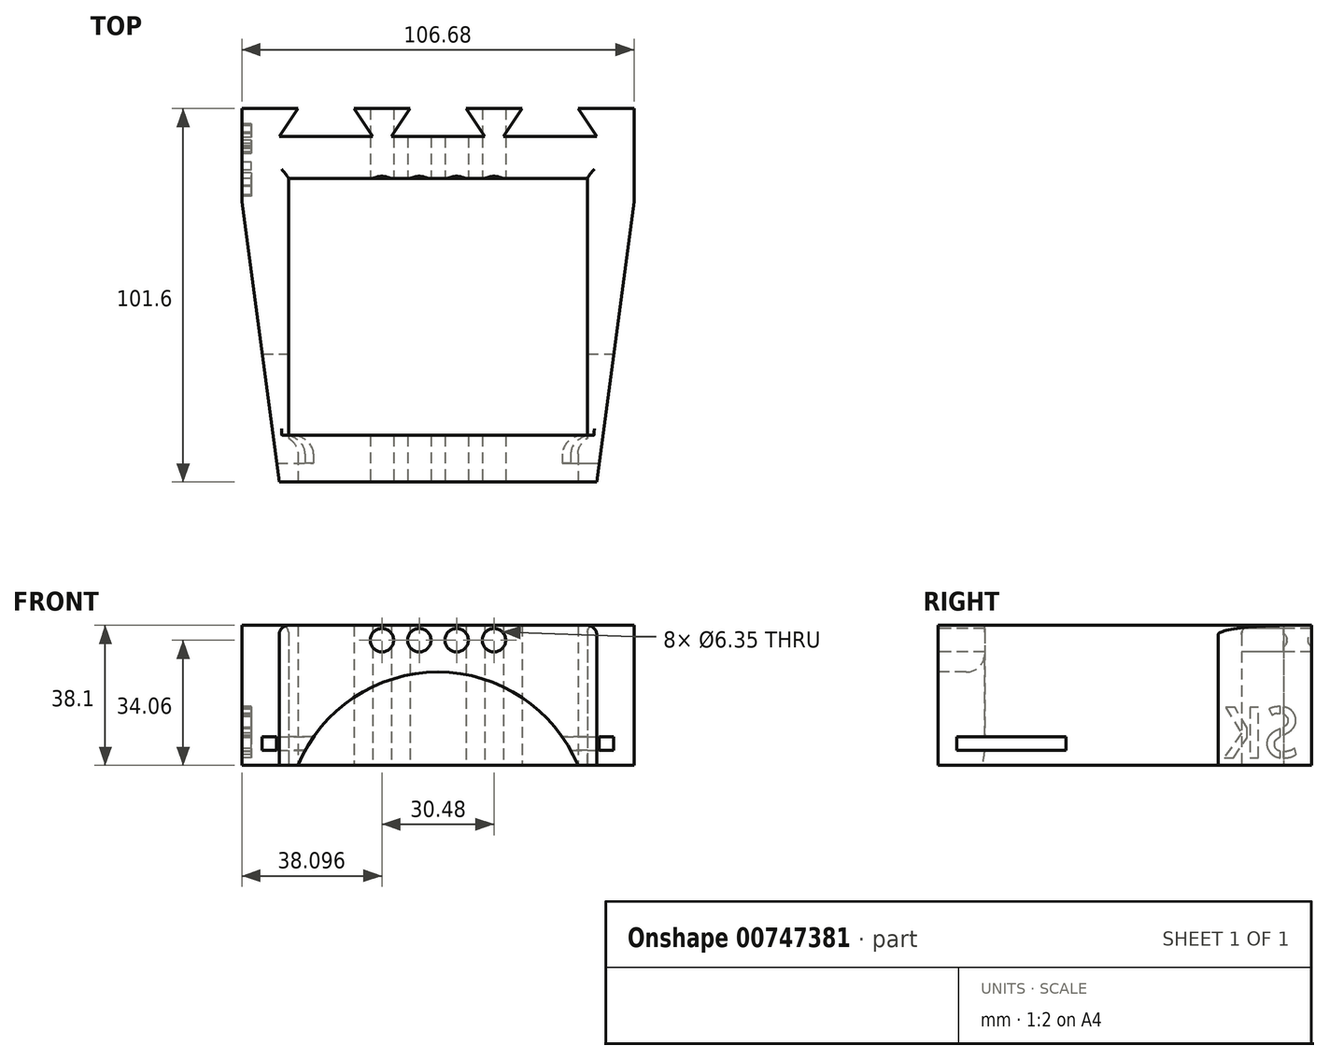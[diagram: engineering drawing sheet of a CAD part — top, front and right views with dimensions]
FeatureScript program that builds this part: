
annotation { "Feature Type Name" : "Feature", "Feature Type Description" : "" }
export const myFeature = defineFeature(function(context is Context, id is Id, definition is map)
    precondition{}
    {
        {
            var Q0;
            Q0=qCreatedBy(makeId("Top.planeOp"),FACE);
            var sketch = newSketch(context, id + "F0", { "sketchPlane" : qUnion([Q0])});
            skLineSegment(sketch, "E0.bottom", {"start": v(-50, 51.06) * mm, "end": v(-34.76, 51.06) * mm});
            skLineSegment(sketch, "E0.top", {"start": v(-50, -50.54) * mm, "end": v(56.68, -50.54) * mm});
            skLineSegment(sketch, "E0.left", {"start": v(-50, 51.06) * mm, "end": v(-50, -50.54) * mm});
            skLineSegment(sketch, "E0.right", {"start": v(56.68, 51.06) * mm, "end": v(56.68, -50.54) * mm});
            skLineSegment(sketch, "E1.bottom", {"start": v(-37.3, 32) * mm, "end": v(43.98, 32) * mm});
            skLineSegment(sketch, "E1.top", {"start": v(-37.3, -37.84) * mm, "end": v(43.98, -37.84) * mm});
            skLineSegment(sketch, "E1.left", {"start": v(-37.3, 32) * mm, "end": v(-37.3, -37.84) * mm});
            skLineSegment(sketch, "E1.right", {"start": v(43.98, 32) * mm, "end": v(43.98, -37.84) * mm});
            skLineSegment(sketch, "E2", {"start": v(-34.76, 51.06) * mm, "end": v(-39.84, 43.44) * mm});
            skLineSegment(sketch, "E3", {"start": v(-39.84, 43.44) * mm, "end": v(-14.44, 43.44) * mm});
            skLineSegment(sketch, "E4", {"start": v(-14.44, 43.44) * mm, "end": v(-19.52, 51.06) * mm});
            skLineSegment(sketch, "E5", {"start": v(-4.28, 51.06) * mm, "end": v(-9.36, 43.44) * mm});
            skLineSegment(sketch, "E6", {"start": v(-9.36, 43.44) * mm, "end": v(16.04, 43.44) * mm});
            skLineSegment(sketch, "E7", {"start": v(16.04, 43.44) * mm, "end": v(10.96, 51.06) * mm});
            skLineSegment(sketch, "E8", {"start": v(26.2, 51.06) * mm, "end": v(21.12, 43.44) * mm});
            skLineSegment(sketch, "E9", {"start": v(21.12, 43.44) * mm, "end": v(46.52, 43.44) * mm});
            skLineSegment(sketch, "E10", {"start": v(46.52, 43.44) * mm, "end": v(41.44, 51.06) * mm});
            skLineSegment(sketch, "E11.trimOffspring", {"start": v(-19.52, 51.06) * mm, "end": v(-4.28, 51.06) * mm});
            skLineSegment(sketch, "E12.trimOffspring", {"start": v(10.96, 51.06) * mm, "end": v(26.2, 51.06) * mm});
            skLineSegment(sketch, "E13.trimOffspring", {"start": v(41.44, 51.06) * mm, "end": v(56.68, 51.06) * mm});
            skSolve(sketch);
        }
        {
            var Q0;
            Q0=makeQuery(id+"F0.imprint","IMPRINT",FACE,{"disambiguationData":[TD([[makeQuery(id+"F0.imprint","IMPRINT",EDGE,{"derivedFrom":sQuery(id+"F0.wireOp",EDGE,"E0.bottom")}),-1.0]])]});
            extrude(context, id + "F1", {"entities" : qUnion([Q0]), "depth" : 38.1 * mm, "offsetDistance" : 25.4 * mm});
        }
        {
            var Q0;
            Q0=makeQuery(id+"F1.opExtrude","SWEPT_FACE",FACE,{"disambiguationData":[OSD([sQuery(id+"F0.wireOp",EDGE,"E0.top")])]});
            var sketch = newSketch(context, id + "F2", { "sketchPlane" : qUnion([Q0])});
            skArc(sketch, "E14", {"start": v(41.44, 0) * mm, "mid": v(3.34, 25.4) * mm, "end": v(-34.76, 0) * mm});
            skSolve(sketch);
        }
        {
            var Q0;
            {var subQ0=sQuery(id+"F2.wireOp",EDGE,"E14");Q0=makeQuery(id+"F2.imprint","IMPRINT",FACE,{"disambiguationData":[TD([[makeQuery(id+"F2.imprint","IMPRINT",EDGE,{"derivedFrom":subQ0}),1.0]])]});}
            extrude(context, id + "F3", {"entities" : qUnion([Q0]), "operationType" : NewBodyOperationType.REMOVE, "oppositeDirection" : true, "depth" : 25.4 * mm, "offsetDistance" : 25.4 * mm});
        }
        {
            var Q0;
            Q0=makeQuery(id+"F3.boolean.opBoolean","COPY",EDGE,{"derivedFrom":makeQuery(id+"F3.opExtrude","CAP_EDGE",EDGE,{"disambiguationData":[OSD([sQuery(id+"F2.wireOp",EDGE,"E14")])],"isStart":true})});
            var Q1;
            Q1=makeQuery(id+"F3.boolean.opBoolean","INTERSECT",EDGE,{"derivedFrom":[makeQuery(id+"F1.opExtrude","SWEPT_FACE",FACE,{"disambiguationData":[OSD([sQuery(id+"F0.wireOp",EDGE,"E1.top")])]}),makeQuery(id+"F3.opExtrude","SWEPT_FACE",FACE,{"disambiguationData":[OSD([sQuery(id+"F2.wireOp",EDGE,"E14")])]})]});
            fillet(context, id + "F4", {"entities" : qUnion([Q0, Q1]), "radius" : 5.08 * mm, "tangentPropagation" : true, "allowEdgeOverflow" : false});
        }
        {
            var Q0;
            Q0=makeQuery(id+"F1.opExtrude","SWEPT_EDGE",EDGE,{"disambiguationData":[OSD([sQuery(id+"F0.wireOp",EDGE,"E0.top"),sQuery(id+"F0.wireOp",EDGE,"E0.left")])]});
            var Q1;
            Q1=makeQuery(id+"F1.opExtrude","SWEPT_EDGE",EDGE,{"disambiguationData":[OSD([sQuery(id+"F0.wireOp",EDGE,"E0.top"),sQuery(id+"F0.wireOp",EDGE,"E0.right")])]});
            chamfer(context, id + "F5", {"entities" : qUnion([Q0, Q1]), "chamferType" : ChamferType.TWO_OFFSETS, "width1" : 10.16 * mm, "oppositeDirection" : false, "width2" : 76.2 * mm, "tangentPropagation" : true});
        }
        {
            var Q0;
            {var subQ0=sQuery(id+"F0.wireOp",EDGE,"E0.right");var subQ1=sQuery(id+"F0.wireOp",EDGE,"E0.top");Q0=makeQuery(id+"F5.opChamfer","BLEND_EDGE",EDGE,{"blendedFrom":[makeQuery(id+"F1.opExtrude","SWEPT_EDGE",EDGE,{"disambiguationData":[OSD([subQ1,subQ0])]}),makeQuery(id+"F1.opExtrude","CAP_FACE",FACE,{"disambiguationData":[OSD([sQuery(id+"F0.wireOp",EDGE,"E0.bottom"),subQ1,sQuery(id+"F0.wireOp",EDGE,"E0.left"),subQ0,sQuery(id+"F0.wireOp",EDGE,"E1.bottom"),sQuery(id+"F0.wireOp",EDGE,"E1.top"),sQuery(id+"F0.wireOp",EDGE,"E1.left"),sQuery(id+"F0.wireOp",EDGE,"E1.right"),sQuery(id+"F0.wireOp",EDGE,"E2"),sQuery(id+"F0.wireOp",EDGE,"E3"),sQuery(id+"F0.wireOp",EDGE,"E4"),sQuery(id+"F0.wireOp",EDGE,"E5"),sQuery(id+"F0.wireOp",EDGE,"E6"),sQuery(id+"F0.wireOp",EDGE,"E7"),sQuery(id+"F0.wireOp",EDGE,"E8"),sQuery(id+"F0.wireOp",EDGE,"E9"),sQuery(id+"F0.wireOp",EDGE,"E10"),sQuery(id+"F0.wireOp",EDGE,"E11.trimOffspring"),sQuery(id+"F0.wireOp",EDGE,"E12.trimOffspring"),sQuery(id+"F0.wireOp",EDGE,"E13.trimOffspring")])],"isStart":false})],"blendedInto":[makeQuery(id+"F1.opExtrude","CAP_FACE",FACE,{"disambiguationData":[OSD([sQuery(id+"F0.wireOp",EDGE,"E0.bottom"),subQ1,sQuery(id+"F0.wireOp",EDGE,"E0.left"),subQ0,sQuery(id+"F0.wireOp",EDGE,"E1.bottom"),sQuery(id+"F0.wireOp",EDGE,"E1.top"),sQuery(id+"F0.wireOp",EDGE,"E1.left"),sQuery(id+"F0.wireOp",EDGE,"E1.right"),sQuery(id+"F0.wireOp",EDGE,"E2"),sQuery(id+"F0.wireOp",EDGE,"E3"),sQuery(id+"F0.wireOp",EDGE,"E4"),sQuery(id+"F0.wireOp",EDGE,"E5"),sQuery(id+"F0.wireOp",EDGE,"E6"),sQuery(id+"F0.wireOp",EDGE,"E7"),sQuery(id+"F0.wireOp",EDGE,"E8"),sQuery(id+"F0.wireOp",EDGE,"E9"),sQuery(id+"F0.wireOp",EDGE,"E10"),sQuery(id+"F0.wireOp",EDGE,"E11.trimOffspring"),sQuery(id+"F0.wireOp",EDGE,"E12.trimOffspring"),sQuery(id+"F0.wireOp",EDGE,"E13.trimOffspring")])],"isStart":false})]});}
            var Q1;
            {var subQ0=sQuery(id+"F0.wireOp",EDGE,"E0.left");var subQ1=sQuery(id+"F0.wireOp",EDGE,"E0.top");Q1=makeQuery(id+"F5.opChamfer","BLEND_EDGE",EDGE,{"blendedFrom":[makeQuery(id+"F1.opExtrude","SWEPT_EDGE",EDGE,{"disambiguationData":[OSD([subQ1,subQ0])]}),makeQuery(id+"F1.opExtrude","CAP_FACE",FACE,{"disambiguationData":[OSD([sQuery(id+"F0.wireOp",EDGE,"E0.bottom"),subQ1,subQ0,sQuery(id+"F0.wireOp",EDGE,"E0.right"),sQuery(id+"F0.wireOp",EDGE,"E1.bottom"),sQuery(id+"F0.wireOp",EDGE,"E1.top"),sQuery(id+"F0.wireOp",EDGE,"E1.left"),sQuery(id+"F0.wireOp",EDGE,"E1.right"),sQuery(id+"F0.wireOp",EDGE,"E2"),sQuery(id+"F0.wireOp",EDGE,"E3"),sQuery(id+"F0.wireOp",EDGE,"E4"),sQuery(id+"F0.wireOp",EDGE,"E5"),sQuery(id+"F0.wireOp",EDGE,"E6"),sQuery(id+"F0.wireOp",EDGE,"E7"),sQuery(id+"F0.wireOp",EDGE,"E8"),sQuery(id+"F0.wireOp",EDGE,"E9"),sQuery(id+"F0.wireOp",EDGE,"E10"),sQuery(id+"F0.wireOp",EDGE,"E11.trimOffspring"),sQuery(id+"F0.wireOp",EDGE,"E12.trimOffspring"),sQuery(id+"F0.wireOp",EDGE,"E13.trimOffspring")])],"isStart":false})],"blendedInto":[makeQuery(id+"F1.opExtrude","CAP_FACE",FACE,{"disambiguationData":[OSD([sQuery(id+"F0.wireOp",EDGE,"E0.bottom"),subQ1,subQ0,sQuery(id+"F0.wireOp",EDGE,"E0.right"),sQuery(id+"F0.wireOp",EDGE,"E1.bottom"),sQuery(id+"F0.wireOp",EDGE,"E1.top"),sQuery(id+"F0.wireOp",EDGE,"E1.left"),sQuery(id+"F0.wireOp",EDGE,"E1.right"),sQuery(id+"F0.wireOp",EDGE,"E2"),sQuery(id+"F0.wireOp",EDGE,"E3"),sQuery(id+"F0.wireOp",EDGE,"E4"),sQuery(id+"F0.wireOp",EDGE,"E5"),sQuery(id+"F0.wireOp",EDGE,"E6"),sQuery(id+"F0.wireOp",EDGE,"E7"),sQuery(id+"F0.wireOp",EDGE,"E8"),sQuery(id+"F0.wireOp",EDGE,"E9"),sQuery(id+"F0.wireOp",EDGE,"E10"),sQuery(id+"F0.wireOp",EDGE,"E11.trimOffspring"),sQuery(id+"F0.wireOp",EDGE,"E12.trimOffspring"),sQuery(id+"F0.wireOp",EDGE,"E13.trimOffspring")])],"isStart":false})]});}
            var Q2;
            Q2=makeQuery(id+"F1.opExtrude","CAP_EDGE",EDGE,{"disambiguationData":[OSD([sQuery(id+"F0.wireOp",EDGE,"E1.bottom")])],"isStart":false});
            fillet(context, id + "F6", {"entities" : qUnion([Q0, Q1, Q2]), "radius" : 2.54 * mm, "tangentPropagation" : true, "allowEdgeOverflow" : false});
        }
        {
            var Q0;
            Q0=makeQuery(id+"F1.opExtrude","SWEPT_FACE",FACE,{"disambiguationData":[OSD([sQuery(id+"F0.wireOp",EDGE,"E0.right")])]});
            var sketch = newSketch(context, id + "F7", { "sketchPlane" : qUnion([Q0])});
            skLineSegment(sketch, "E15.bottom", {"start": v(-45.48, 7.73) * mm, "end": v(-15.77, 7.73) * mm});
            skLineSegment(sketch, "E15.top", {"start": v(-45.48, 4.07) * mm, "end": v(-15.77, 4.07) * mm});
            skLineSegment(sketch, "E15.left", {"start": v(-15.77, 7.73) * mm, "end": v(-15.77, 4.07) * mm});
            skLineSegment(sketch, "E15.right", {"start": v(-45.48, 7.73) * mm, "end": v(-45.48, 4.07) * mm});
            skSolve(sketch);
        }
        {
            var Q0;
            Q0=makeQuery(id+"F7.imprint","IMPRINT",FACE,{"disambiguationData":[TD([[makeQuery(id+"F7.imprint","IMPRINT",EDGE,{"derivedFrom":sQuery(id+"F7.wireOp",EDGE,"E15.bottom")}),-1.0]])]});
            extrude(context, id + "F8", {"entities" : qUnion([Q0]), "operationType" : NewBodyOperationType.REMOVE, "oppositeDirection" : true, "depth" : 203.2 * mm, "offsetDistance" : 25.4 * mm});
        }
        {
            var Q0;
            Q0=makeQuery(id+"F1.opExtrude","SWEPT_FACE",FACE,{"disambiguationData":[OSD([sQuery(id+"F0.wireOp",EDGE,"E0.top")])]});
            var sketch = newSketch(context, id + "F9", { "sketchPlane" : qUnion([Q0])});
            skPoint(sketch, "E16", {"position": v(-11.9, 34.06) * mm});
            skPoint(sketch, "E17", {"position": v(-1.74, 34.06) * mm});
            skPoint(sketch, "E18", {"position": v(8.42, 34.06) * mm});
            skPoint(sketch, "E19", {"position": v(18.58, 34.06) * mm});
            skPoint(sketch, "E20.positionSnap0", {"position": v(3.34, 30.48) * mm});
            skSolve(sketch);
        }
        {
            var Q0;
            Q0=sQuery(id+"F9.wireOp",VERTEX,"E16");
            var Q1;
            Q1=sQuery(id+"F9.wireOp",VERTEX,"E17");
            var Q2;
            Q2=sQuery(id+"F9.wireOp",VERTEX,"E18");
            var Q3;
            Q3=sQuery(id+"F9.wireOp",VERTEX,"E19");
            var Q4;
            Q4=makeQuery(id+"F1.opExtrude","SWEPT_BODY",BODY,{"disambiguationData":[OSD([sQuery(id+"F0.wireOp",EDGE,"E0.bottom"),sQuery(id+"F0.wireOp",EDGE,"E0.top"),sQuery(id+"F0.wireOp",EDGE,"E0.left"),sQuery(id+"F0.wireOp",EDGE,"E0.right"),sQuery(id+"F0.wireOp",EDGE,"E1.bottom"),sQuery(id+"F0.wireOp",EDGE,"E1.top"),sQuery(id+"F0.wireOp",EDGE,"E1.left"),sQuery(id+"F0.wireOp",EDGE,"E1.right"),sQuery(id+"F0.wireOp",EDGE,"E2"),sQuery(id+"F0.wireOp",EDGE,"E3"),sQuery(id+"F0.wireOp",EDGE,"E4"),sQuery(id+"F0.wireOp",EDGE,"E5"),sQuery(id+"F0.wireOp",EDGE,"E6"),sQuery(id+"F0.wireOp",EDGE,"E7"),sQuery(id+"F0.wireOp",EDGE,"E8"),sQuery(id+"F0.wireOp",EDGE,"E9"),sQuery(id+"F0.wireOp",EDGE,"E10"),sQuery(id+"F0.wireOp",EDGE,"E11.trimOffspring"),sQuery(id+"F0.wireOp",EDGE,"E12.trimOffspring"),sQuery(id+"F0.wireOp",EDGE,"E13.trimOffspring")])]});
            hole(context, id + "F10", {"style" : HoleStyle.SIMPLE, "endStyle" : HoleEndStyle.BLIND, "holeDiameter" : 6.35 * mm, "majorDiameter" : 6.35 * mm, "holeDepth" : 203.2 * mm, "isTappedThrough" : true, "tappedDepth" : 12.7 * mm, "tapClearance" : 3, "locations" : qUnion([Q0, Q1, Q2, Q3]), "scope" : qUnion([Q4])});
        }
        {
            var Q0;
            {var subQ0=sQuery(id+"F0.wireOp",EDGE,"E1.right");var subQ1=sQuery(id+"F0.wireOp",EDGE,"E0.right");var subQ2=sQuery(id+"F0.wireOp",EDGE,"E0.top");Q0=makeQuery(id+"F6.opFillet","BLEND_EDGE",EDGE,{"blendedFrom":[makeQuery(id+"F5.opChamfer","BLEND_EDGE",EDGE,{"blendedFrom":[makeQuery(id+"F1.opExtrude","SWEPT_EDGE",EDGE,{"disambiguationData":[OSD([subQ2,subQ1])]}),makeQuery(id+"F1.opExtrude","CAP_FACE",FACE,{"disambiguationData":[OSD([sQuery(id+"F0.wireOp",EDGE,"E0.bottom"),subQ2,sQuery(id+"F0.wireOp",EDGE,"E0.left"),subQ1,sQuery(id+"F0.wireOp",EDGE,"E1.bottom"),sQuery(id+"F0.wireOp",EDGE,"E1.top"),sQuery(id+"F0.wireOp",EDGE,"E1.left"),subQ0,sQuery(id+"F0.wireOp",EDGE,"E2"),sQuery(id+"F0.wireOp",EDGE,"E3"),sQuery(id+"F0.wireOp",EDGE,"E4"),sQuery(id+"F0.wireOp",EDGE,"E5"),sQuery(id+"F0.wireOp",EDGE,"E6"),sQuery(id+"F0.wireOp",EDGE,"E7"),sQuery(id+"F0.wireOp",EDGE,"E8"),sQuery(id+"F0.wireOp",EDGE,"E9"),sQuery(id+"F0.wireOp",EDGE,"E10"),sQuery(id+"F0.wireOp",EDGE,"E11.trimOffspring"),sQuery(id+"F0.wireOp",EDGE,"E12.trimOffspring"),sQuery(id+"F0.wireOp",EDGE,"E13.trimOffspring")])],"isStart":false})],"blendedInto":[makeQuery(id+"F1.opExtrude","CAP_FACE",FACE,{"disambiguationData":[OSD([sQuery(id+"F0.wireOp",EDGE,"E0.bottom"),subQ2,sQuery(id+"F0.wireOp",EDGE,"E0.left"),subQ1,sQuery(id+"F0.wireOp",EDGE,"E1.bottom"),sQuery(id+"F0.wireOp",EDGE,"E1.top"),sQuery(id+"F0.wireOp",EDGE,"E1.left"),subQ0,sQuery(id+"F0.wireOp",EDGE,"E2"),sQuery(id+"F0.wireOp",EDGE,"E3"),sQuery(id+"F0.wireOp",EDGE,"E4"),sQuery(id+"F0.wireOp",EDGE,"E5"),sQuery(id+"F0.wireOp",EDGE,"E6"),sQuery(id+"F0.wireOp",EDGE,"E7"),sQuery(id+"F0.wireOp",EDGE,"E8"),sQuery(id+"F0.wireOp",EDGE,"E9"),sQuery(id+"F0.wireOp",EDGE,"E10"),sQuery(id+"F0.wireOp",EDGE,"E11.trimOffspring"),sQuery(id+"F0.wireOp",EDGE,"E12.trimOffspring"),sQuery(id+"F0.wireOp",EDGE,"E13.trimOffspring")])],"isStart":false})]}),makeQuery(id+"F1.opExtrude","SWEPT_FACE",FACE,{"disambiguationData":[OSD([subQ0])]})],"blendedInto":[makeQuery(id+"F1.opExtrude","SWEPT_FACE",FACE,{"disambiguationData":[OSD([subQ0])]})]});}
            var Q1;
            {var subQ0=sQuery(id+"F0.wireOp",EDGE,"E1.left");var subQ1=sQuery(id+"F0.wireOp",EDGE,"E0.left");var subQ2=sQuery(id+"F0.wireOp",EDGE,"E0.top");Q1=makeQuery(id+"F6.opFillet","BLEND_EDGE",EDGE,{"blendedFrom":[makeQuery(id+"F5.opChamfer","BLEND_EDGE",EDGE,{"blendedFrom":[makeQuery(id+"F1.opExtrude","SWEPT_EDGE",EDGE,{"disambiguationData":[OSD([subQ2,subQ1])]}),makeQuery(id+"F1.opExtrude","CAP_FACE",FACE,{"disambiguationData":[OSD([sQuery(id+"F0.wireOp",EDGE,"E0.bottom"),subQ2,subQ1,sQuery(id+"F0.wireOp",EDGE,"E0.right"),sQuery(id+"F0.wireOp",EDGE,"E1.bottom"),sQuery(id+"F0.wireOp",EDGE,"E1.top"),subQ0,sQuery(id+"F0.wireOp",EDGE,"E1.right"),sQuery(id+"F0.wireOp",EDGE,"E2"),sQuery(id+"F0.wireOp",EDGE,"E3"),sQuery(id+"F0.wireOp",EDGE,"E4"),sQuery(id+"F0.wireOp",EDGE,"E5"),sQuery(id+"F0.wireOp",EDGE,"E6"),sQuery(id+"F0.wireOp",EDGE,"E7"),sQuery(id+"F0.wireOp",EDGE,"E8"),sQuery(id+"F0.wireOp",EDGE,"E9"),sQuery(id+"F0.wireOp",EDGE,"E10"),sQuery(id+"F0.wireOp",EDGE,"E11.trimOffspring"),sQuery(id+"F0.wireOp",EDGE,"E12.trimOffspring"),sQuery(id+"F0.wireOp",EDGE,"E13.trimOffspring")])],"isStart":false})],"blendedInto":[makeQuery(id+"F1.opExtrude","CAP_FACE",FACE,{"disambiguationData":[OSD([sQuery(id+"F0.wireOp",EDGE,"E0.bottom"),subQ2,subQ1,sQuery(id+"F0.wireOp",EDGE,"E0.right"),sQuery(id+"F0.wireOp",EDGE,"E1.bottom"),sQuery(id+"F0.wireOp",EDGE,"E1.top"),subQ0,sQuery(id+"F0.wireOp",EDGE,"E1.right"),sQuery(id+"F0.wireOp",EDGE,"E2"),sQuery(id+"F0.wireOp",EDGE,"E3"),sQuery(id+"F0.wireOp",EDGE,"E4"),sQuery(id+"F0.wireOp",EDGE,"E5"),sQuery(id+"F0.wireOp",EDGE,"E6"),sQuery(id+"F0.wireOp",EDGE,"E7"),sQuery(id+"F0.wireOp",EDGE,"E8"),sQuery(id+"F0.wireOp",EDGE,"E9"),sQuery(id+"F0.wireOp",EDGE,"E10"),sQuery(id+"F0.wireOp",EDGE,"E11.trimOffspring"),sQuery(id+"F0.wireOp",EDGE,"E12.trimOffspring"),sQuery(id+"F0.wireOp",EDGE,"E13.trimOffspring")])],"isStart":false})]}),makeQuery(id+"F1.opExtrude","SWEPT_FACE",FACE,{"disambiguationData":[OSD([subQ0])]})],"blendedInto":[makeQuery(id+"F1.opExtrude","SWEPT_FACE",FACE,{"disambiguationData":[OSD([subQ0])]})]});}
            var Q2;
            Q2=makeQuery(id+"F1.opExtrude","CAP_EDGE",EDGE,{"disambiguationData":[OSD([sQuery(id+"F0.wireOp",EDGE,"E1.right")])],"isStart":false});
            var Q3;
            Q3=makeQuery(id+"F1.opExtrude","CAP_EDGE",EDGE,{"disambiguationData":[OSD([sQuery(id+"F0.wireOp",EDGE,"E1.left")])],"isStart":false});
            fillet(context, id + "F11", {"entities" : qUnion([Q0, Q1, Q2, Q3]), "radius" : 1.9 * mm, "tangentPropagation" : true, "allowEdgeOverflow" : false});
        }
        {
            var Q0;
            Q0=makeQuery(id+"F1.opExtrude","SWEPT_FACE",FACE,{"disambiguationData":[OSD([sQuery(id+"F0.wireOp",EDGE,"E0.left")])]});
            var sketch = newSketch(context, id + "F12", { "sketchPlane" : qUnion([Q0])});
            skText(sketch, "E21", { "text": "SK", "fontName": "AllertaStencil-Regular.ttf"});
            const initialGuessF12  = {"E21": [-0.04835, 0.0021, 1, 0, 0.01371]};
            skSetInitialGuess(sketch, initialGuessF12);
            skSolve(sketch);
        }
        {
            var Q0;
            Q0 = qSketchRegion(id + "F12", true);
            extrude(context, id + "F13", {"entities" : qUnion([Q0]), "operationType" : NewBodyOperationType.REMOVE, "oppositeDirection" : true, "depth" : 2.54 * mm, "offsetDistance" : 25.4 * mm});
        }
    });
